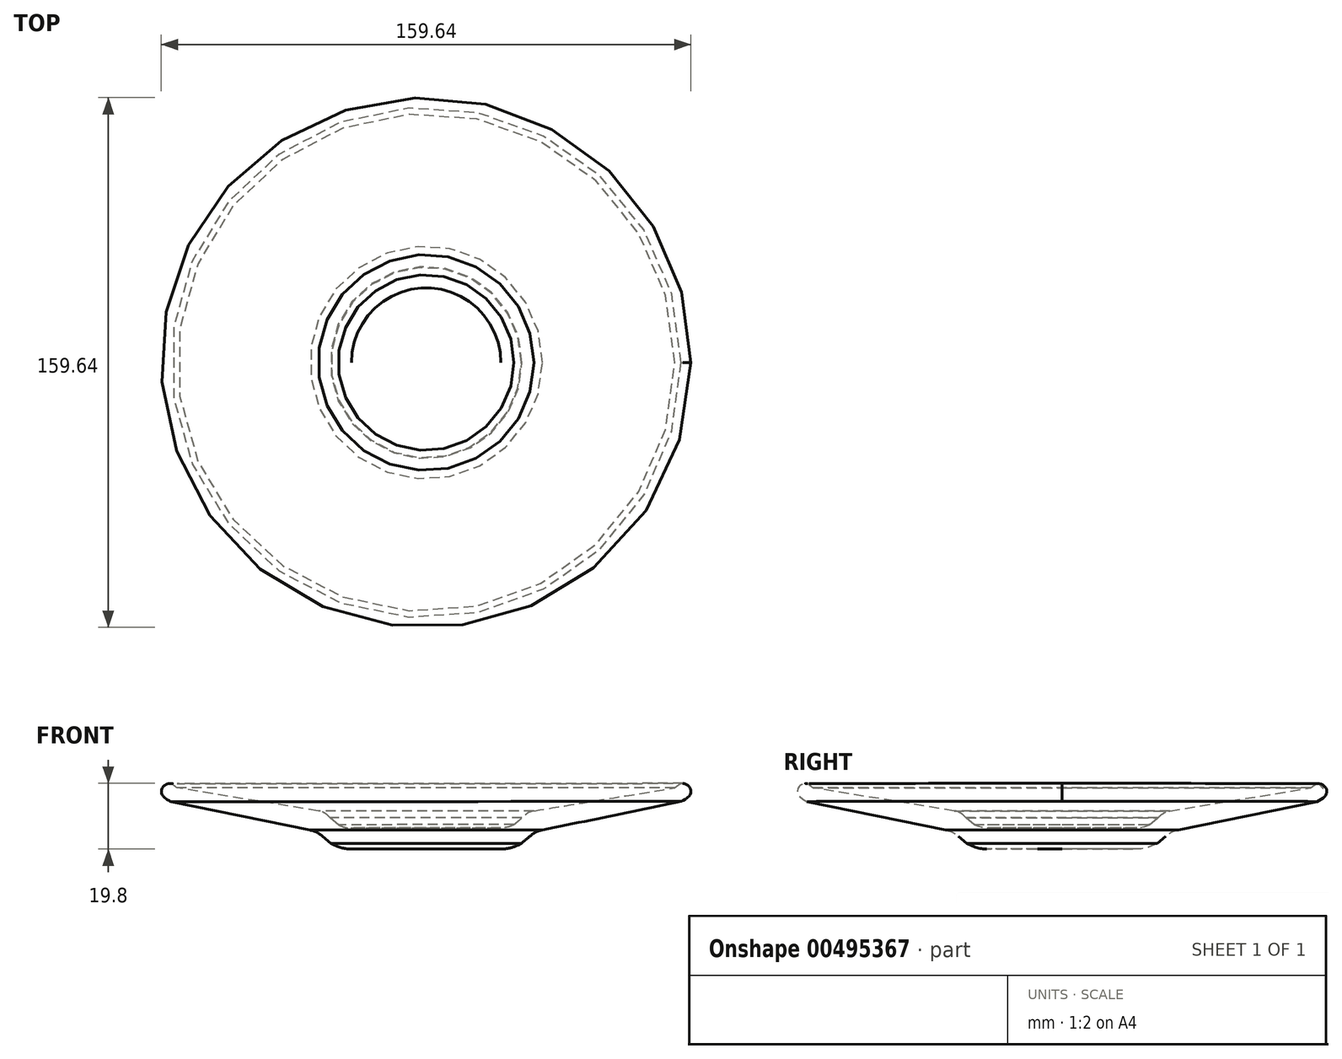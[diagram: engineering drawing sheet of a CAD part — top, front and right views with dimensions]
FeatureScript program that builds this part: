
annotation { "Feature Type Name" : "Feature", "Feature Type Description" : "" }
export const myFeature = defineFeature(function(context is Context, id is Id, definition is map)
    precondition{}
    {
        {
            var Q0;
            Q0=qCreatedBy(makeId("Front.planeOp"),FACE);
            var sketch = newSketch(context, id + "F0", { "sketchPlane" : qUnion([Q0])});
            skLineSegment(sketch, "E0", {"start": v(-38.24, -8.5) * mm, "end": v(-15.51, -8.49) * mm});
            skFitSpline(sketch, "E1", {"points": [v(-15.51, -8.49) * mm, v(-9.56, -6.8) * mm], "startDerivative": vector(6.27, 0) * mm, "endDerivative": vector(4.76, 2.68) * mm});
            skLineSegment(sketch, "E2", {"start": v(-9.56, -6.8) * mm, "end": v(-6.98, -4.62) * mm});
            skFitSpline(sketch, "E3", {"points": [v(-6.98, -4.62) * mm, v(-3.2, -2.76) * mm], "startDerivative": vector(4.12, 3.51) * mm, "endDerivative": vector(4.13, 0.57) * mm});
            skLineSegment(sketch, "E4", {"start": v(-3.2, -2.76) * mm, "end": v(38.6, 5.86) * mm});
            skFitSpline(sketch, "E5", {"points": [v(38.6, 5.86) * mm, v(39.16, 11.3) * mm], "startDerivative": vector(15.91, 6.96) * mm, "endDerivative": vector(-5, 0) * mm});
            skFitSpline(sketch, "E6", {"points": [v(39.16, 11.3) * mm, v(36.71, 9.98) * mm], "startDerivative": vector(-3.3, 0) * mm, "endDerivative": vector(-2.95, -1.69) * mm});
            skLineSegment(sketch, "E7", {"start": v(36.71, 9.98) * mm, "end": v(-5.72, 3.03) * mm});
            skFitSpline(sketch, "E8", {"points": [v(-5.72, 3.03) * mm, v(-9.34, 0.92) * mm], "startDerivative": vector(-5.28, -0.78) * mm, "endDerivative": vector(-2.88, -2.99) * mm});
            skLineSegment(sketch, "E9", {"start": v(-9.34, 0.92) * mm, "end": v(-11.76, -1.14) * mm});
            skFitSpline(sketch, "E10", {"points": [v(-11.76, -1.14) * mm, v(-15.73, -2.13) * mm], "startDerivative": vector(-2.15, -1.03) * mm, "endDerivative": vector(-5.84, 0.16) * mm});
            skLineSegment(sketch, "E11", {"start": v(-15.73, -2.13) * mm, "end": v(-38.24, -2.13) * mm});
            skLineSegment(sketch, "E12", {"start": v(-38.24, -2.13) * mm, "end": v(-38.24, -8.5) * mm});
            skSolve(sketch);
        }
        {
            var Q0;
            Q0=makeQuery(id+"F0.imprint","IMPRINT",FACE,{"disambiguationData":[TD([[makeQuery(id+"F0.imprint","IMPRINT",EDGE,{"derivedFrom":sQuery(id+"F0.wireOp",EDGE,"E0")}),1.0]])]});
            var Q1;
            Q1=sQuery(id+"F0.wireOp",EDGE,"E12");
            revolve(context, id + "F1", {"entities" : qUnion([Q0]), "axis" : qUnion([Q1]), "revolveType" : RevolveType.FULL});
        }
        {
            var Q0;
            Q0=makeQuery(id+"F0.imprint","IMPRINT",FACE,{"disambiguationData":[TD([[makeQuery(id+"F0.imprint","IMPRINT",EDGE,{"derivedFrom":sQuery(id+"F0.wireOp",EDGE,"E0")}),1.0]])]});
            var Q1;
            Q1=sQuery(id+"F0.wireOp",EDGE,"E12");
            revolve(context, id + "F2", {"entities" : qUnion([Q0]), "axis" : qUnion([Q1]), "revolveType" : RevolveType.FULL});
        }
    });
